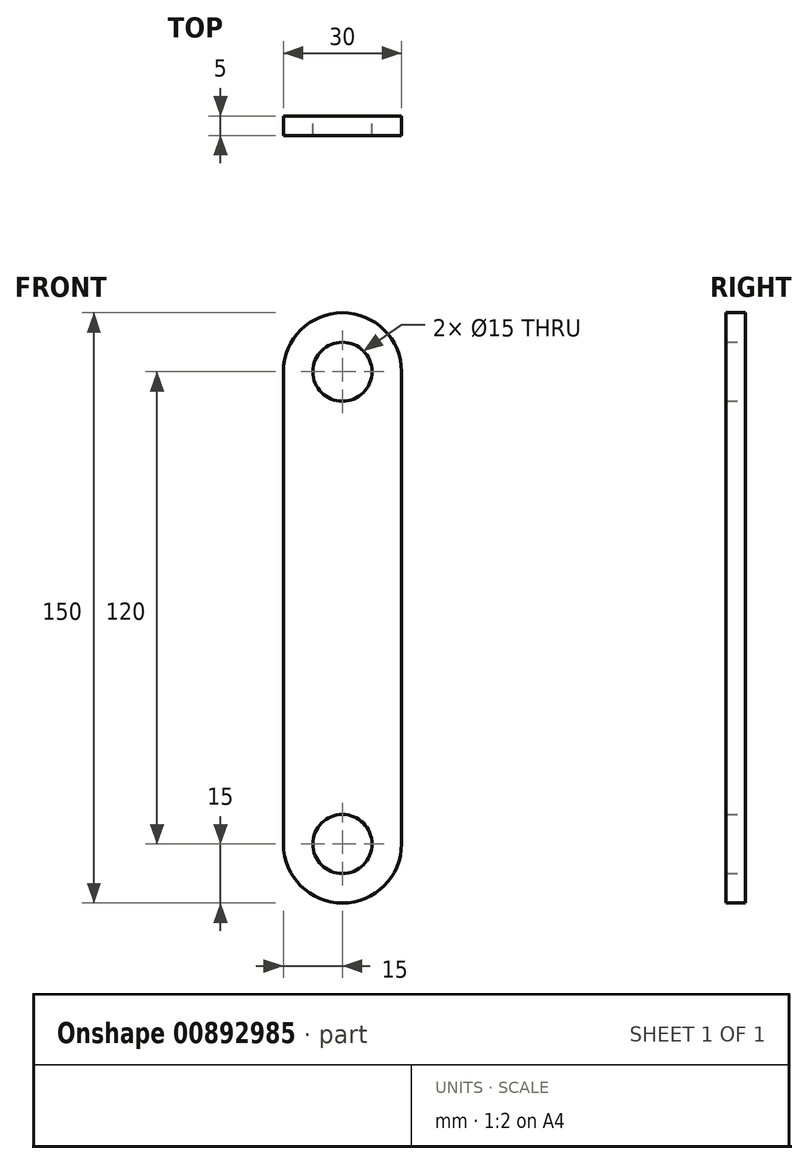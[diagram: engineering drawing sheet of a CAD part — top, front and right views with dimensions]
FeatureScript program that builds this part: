
annotation { "Feature Type Name" : "Feature", "Feature Type Description" : "" }
export const myFeature = defineFeature(function(context is Context, id is Id, definition is map)
    precondition{}
    {
        {
            var Q0;
            Q0=qCreatedBy(makeId("Front.planeOp"),FACE);
            var sketch = newSketch(context, id + "F0", { "sketchPlane" : qUnion([Q0])});
            skCircle(sketch, "E0", {"center": v(0, 60) * mm, "radius": 7.5 * mm});
            skCircle(sketch, "E1", {"center": v(0, -60) * mm, "radius": 7.5 * mm});
            skArc(sketch, "E2", {"start": v(-15, -60) * mm, "mid": v(0, -75) * mm, "end": v(15, -60) * mm});
            skArc(sketch, "E3", {"start": v(15, 60) * mm, "mid": v(0, 75) * mm, "end": v(-15, 60) * mm});
            skLineSegment(sketch, "E4", {"start": v(-15, 60) * mm, "end": v(-15, -60) * mm});
            skLineSegment(sketch, "E5", {"start": v(15, 60) * mm, "end": v(15, -60) * mm});
            skSolve(sketch);
        }
        {
            var Q0;
            Q0 = qSketchRegion(id + "F0", true);
            extrude(context, id + "F1", {"entities" : qUnion([Q0]), "depth" : 5 * mm, "offsetDistance" : 25 * mm});
        }
    });
